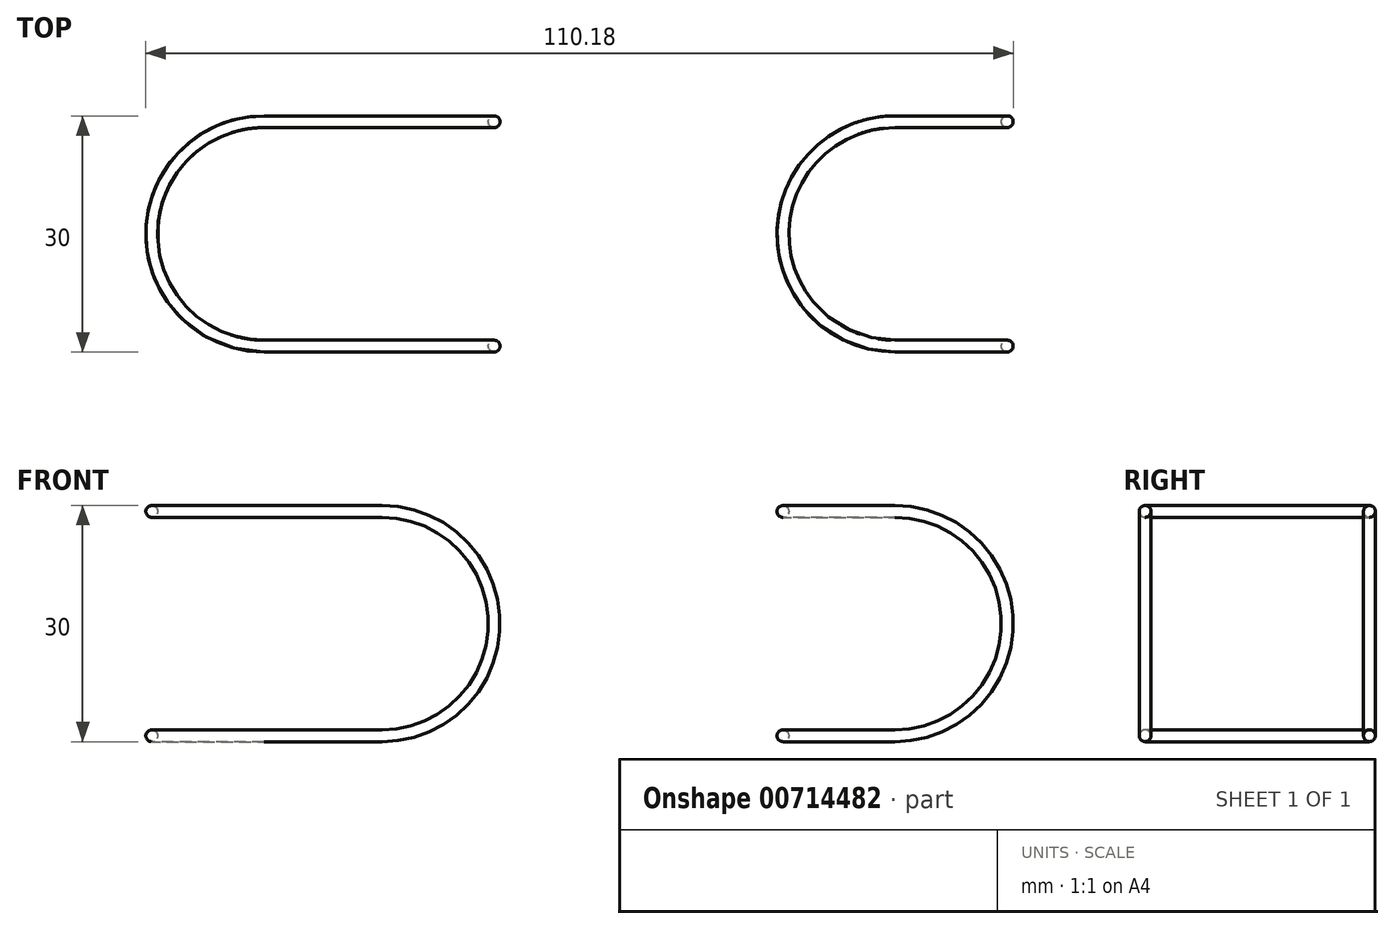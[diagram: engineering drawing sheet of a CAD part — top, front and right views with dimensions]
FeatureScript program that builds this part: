
annotation { "Feature Type Name" : "Feature", "Feature Type Description" : "" }
export const myFeature = defineFeature(function(context is Context, id is Id, definition is map)
    precondition{}
    {
        {
            var Q0;
            Q0=qCreatedBy(makeId("Front.planeOp"),FACE);
            var sketch = newSketch(context, id + "F0", { "sketchPlane" : qUnion([Q0])});
            skArc(sketch, "E0", {"start": v(0, -15) * mm, "mid": v(15, 0) * mm, "end": v(0, 15) * mm});
            skLineSegment(sketch, "E1", {"start": v(0, 15) * mm, "end": v(-30, 15) * mm});
            skLineSegment(sketch, "E2", {"start": v(0, -15) * mm, "end": v(-30, -15) * mm});
            skLineSegment(sketch, "E3", {"start": v(-30, -15) * mm, "end": v(-30, 15) * mm});
            skSolve(sketch);
        }
        {
            var Q0;
            Q0 = qSketchRegion(id + "F0", true);
            extrude(context, id + "F1", {"entities" : qUnion([Q0]), "endBound" : BoundingType.SYMMETRIC, "depth" : 30 * mm, "offsetDistance" : 25 * mm});
        }
        {
            var Q0;
            Q0=makeQuery(id+"F1.opExtrude","CAP_EDGE",EDGE,{"disambiguationData":[OSD([sQuery(id+"F0.wireOp",EDGE,"E3")])],"isStart":false});
            var Q1;
            Q1=makeQuery(id+"F1.opExtrude","CAP_EDGE",EDGE,{"disambiguationData":[OSD([sQuery(id+"F0.wireOp",EDGE,"E3")])],"isStart":true});
            fillet(context, id + "F2", {"entities" : qUnion([Q0, Q1]), "radius" : 15 * mm, "tangentPropagation" : true, "allowEdgeOverflow" : false});
        }
        {
            var Q0;
            Q0=makeQuery(id+"F1.opExtrude","SWEPT_FACE",FACE,{"disambiguationData":[OSD([sQuery(id+"F0.wireOp",EDGE,"E0")])]});
            var Q1;
            Q1=makeQuery(id+"F1.opExtrude","SWEPT_FACE",FACE,{"disambiguationData":[OSD([sQuery(id+"F0.wireOp",EDGE,"E2")])]});
            var Q2;
            Q2=makeQuery(id+"F1.opExtrude","SWEPT_FACE",FACE,{"disambiguationData":[OSD([sQuery(id+"F0.wireOp",EDGE,"E1")])]});
            shell(context, id + "F3", {"entities" : qUnion([Q0, Q1, Q2]), "thickness" : 1.5 * mm});
        }
        {
            var Q0;
            Q0=qCreatedBy(makeId("Front.planeOp"),FACE);
            var sketch = newSketch(context, id + "F4", { "sketchPlane" : qUnion([Q0])});
            skArc(sketch, "E4.0", {"start": v(0, -15) * mm, "mid": v(15, 0) * mm, "end": v(0, 15) * mm, "construction": true});
            skLineSegment(sketch, "E4.1", {"start": v(0, -15) * mm, "end": v(-15, -15) * mm, "construction": true});
            skLineSegment(sketch, "E4.2", {"start": v(0, 15) * mm, "end": v(-15, 15) * mm, "construction": true});
            skLineSegment(sketch, "E4.3", {"start": v(-15, 15) * mm, "end": v(-30, 15) * mm, "construction": true});
            skLineSegment(sketch, "E4.4", {"start": v(-15, -15) * mm, "end": v(-30, -15) * mm, "construction": true});
            skLineSegment(sketch, "E5.0", {"start": v(-15, 13.5) * mm, "end": v(-30, 13.5) * mm});
            skLineSegment(sketch, "E5.1", {"start": v(-15, -13.5) * mm, "end": v(-30, -13.5) * mm});
            skLineSegment(sketch, "E5.2", {"start": v(0, -13.5) * mm, "end": v(-15, -13.5) * mm});
            skArc(sketch, "E5.3", {"start": v(0, -13.5) * mm, "mid": v(13.5, 0) * mm, "end": v(0, 13.5) * mm});
            skLineSegment(sketch, "E5.4", {"start": v(0, 13.5) * mm, "end": v(-15, 13.5) * mm});
            skLineSegment(sketch, "E6", {"start": v(-30, -13.5) * mm, "end": v(-30, 13.5) * mm});
            skSolve(sketch);
        }
        {
            var Q0;
            Q0=makeQuery(id+"F4.imprint","IMPRINT",FACE,{"disambiguationData":[TD([[makeQuery(id+"F4.imprint","IMPRINT",EDGE,{"derivedFrom":sQuery(id+"F4.wireOp",EDGE,"E5.0")}),1.0]])]});
            extrude(context, id + "F5", {"entities" : qUnion([Q0]), "operationType" : NewBodyOperationType.REMOVE, "endBound" : BoundingType.SYMMETRIC, "depth" : 35 * mm, "offsetDistance" : 25 * mm});
        }
        {
            var Q0;
            Q0=makeQuery(id+"F1.opExtrude","CAP_EDGE",EDGE,{"disambiguationData":[OSD([sQuery(id+"F0.wireOp",EDGE,"E1")])],"isStart":true});
            var Q1;
            Q1=makeQuery(id+"F5.boolean.opBoolean","INTERSECT",EDGE,{"derivedFrom":[makeQuery(id+"F1.opExtrude","CAP_FACE",FACE,{"disambiguationData":[OSD([sQuery(id+"F0.wireOp",EDGE,"E0"),sQuery(id+"F0.wireOp",EDGE,"E1"),sQuery(id+"F0.wireOp",EDGE,"E2"),sQuery(id+"F0.wireOp",EDGE,"E3")])],"isStart":true}),makeQuery(id+"F5.opExtrude","SWEPT_FACE",FACE,{"disambiguationData":[OSD([sQuery(id+"F4.wireOp",EDGE,"E5.0"),sQuery(id+"F4.wireOp",EDGE,"E5.4")])]})]});
            var Q2;
            {var subQ0=sQuery(id+"F0.wireOp",EDGE,"E2");Q2=makeQuery(id+"F3.opShell","OFFSET_EDGE",EDGE,{"disambiguationData":[OSD([subQ0]),TDD([makeQuery(id+"F1.opExtrude","CAP_EDGE",EDGE,{"disambiguationData":[OSD([subQ0])],"isStart":false})])]});}
            var Q3;
            {var subQ0=sQuery(id+"F0.wireOp",EDGE,"E3");var subQ1=sQuery(id+"F0.wireOp",EDGE,"E2");var subQ2=sQuery(id+"F0.wireOp",EDGE,"E1");var subQ3=sQuery(id+"F0.wireOp",EDGE,"E0");Q3=makeQuery(id+"F5.boolean.opBoolean","INTERSECT",EDGE,{"derivedFrom":[makeQuery(id+"F3.opShell","OFFSET_FACE",FACE,{"disambiguationData":[OSD([subQ3,subQ2,subQ1,subQ0]),TDD([makeQuery(id+"F1.opExtrude","CAP_FACE",FACE,{"disambiguationData":[OSD([subQ3,subQ2,subQ1,subQ0])],"isStart":false})])]}),makeQuery(id+"F5.opExtrude","SWEPT_FACE",FACE,{"disambiguationData":[OSD([sQuery(id+"F4.wireOp",EDGE,"E5.0"),sQuery(id+"F4.wireOp",EDGE,"E5.4")])]})]});}
            fillet(context, id + "F6", {"entities" : qUnion([Q0, Q1, Q2, Q3]), "radius" : .75 * mm, "tangentPropagation" : true, "allowEdgeOverflow" : false});
        }
        {
            var Q0;
            Q0=qCreatedBy(makeId("Front.planeOp"),FACE);
            var sketch = newSketch(context, id + "F7", { "sketchPlane" : qUnion([Q0])});
            skArc(sketch, "E7", {"start": v(65.18, -15) * mm, "mid": v(80.18, 0) * mm, "end": v(65.18, 15) * mm});
            skLineSegment(sketch, "E8", {"start": v(65.18, 15) * mm, "end": v(50.18, 15) * mm});
            skLineSegment(sketch, "E9", {"start": v(50.18, -15) * mm, "end": v(65.18, -15) * mm});
            skLineSegment(sketch, "E10", {"start": v(50.18, 15) * mm, "end": v(50.18, -15) * mm});
            skSolve(sketch);
        }
        {
            var Q0;
            Q0=makeQuery(id+"F7.imprint","IMPRINT",FACE,{"disambiguationData":[TD([[makeQuery(id+"F7.imprint","IMPRINT",EDGE,{"derivedFrom":sQuery(id+"F7.wireOp",EDGE,"E7")}),1.0]])]});
            extrude(context, id + "F8", {"entities" : qUnion([Q0]), "endBound" : BoundingType.SYMMETRIC, "depth" : 30 * mm, "offsetDistance" : 25 * mm});
        }
        {
            var Q0;
            Q0=makeQuery(id+"F8.opExtrude","CAP_EDGE",EDGE,{"disambiguationData":[OSD([sQuery(id+"F7.wireOp",EDGE,"E10")])],"isStart":true});
            var Q1;
            Q1=makeQuery(id+"F8.opExtrude","CAP_EDGE",EDGE,{"disambiguationData":[OSD([sQuery(id+"F7.wireOp",EDGE,"E10")])],"isStart":false});
            fillet(context, id + "F9", {"entities" : qUnion([Q0, Q1]), "radius" : 15 * mm, "tangentPropagation" : true, "allowEdgeOverflow" : false});
        }
        {
            var Q0;
            Q0=makeQuery(id+"F8.opExtrude","CAP_FACE",FACE,{"disambiguationData":[OSD([sQuery(id+"F7.wireOp",EDGE,"E7"),sQuery(id+"F7.wireOp",EDGE,"E8"),sQuery(id+"F7.wireOp",EDGE,"E9"),sQuery(id+"F7.wireOp",EDGE,"E10")])],"isStart":true});
            var Q1;
            Q1=makeQuery(id+"F9.opFillet","BLEND_FACE",FACE,{"disambiguationData":[OSD([sQuery(id+"F7.wireOp",EDGE,"E10")])]});
            var Q2;
            Q2=makeQuery(id+"F8.opExtrude","CAP_FACE",FACE,{"disambiguationData":[OSD([sQuery(id+"F7.wireOp",EDGE,"E7"),sQuery(id+"F7.wireOp",EDGE,"E8"),sQuery(id+"F7.wireOp",EDGE,"E9"),sQuery(id+"F7.wireOp",EDGE,"E10")])],"isStart":false});
            shell(context, id + "F10", {"entities" : qUnion([Q0, Q1, Q2]), "thickness" : 1.5 * mm});
        }
        {
            var Q0;
            Q0=makeQuery(id+"F8.opExtrude","SWEPT_FACE",FACE,{"disambiguationData":[OSD([sQuery(id+"F7.wireOp",EDGE,"E7")])]});
            var Q1;
            Q1=makeQuery(id+"F8.opExtrude","SWEPT_FACE",FACE,{"disambiguationData":[OSD([sQuery(id+"F7.wireOp",EDGE,"E9")])]});
            var Q2;
            Q2=makeQuery(id+"F8.opExtrude","SWEPT_FACE",FACE,{"disambiguationData":[OSD([sQuery(id+"F7.wireOp",EDGE,"E8")])]});
            shell(context, id + "F11", {"entities" : qUnion([Q0, Q1, Q2]), "thickness" : 1.5 * mm});
        }
        {
            var Q0;
            Q0=qCreatedBy(makeId("Top.planeOp"),FACE);
            var sketch = newSketch(context, id + "F12", { "sketchPlane" : qUnion([Q0])});
            skLineSegment(sketch, "E11.0", {"start": v(65.18, 15) * mm, "end": v(80.18, 15) * mm, "construction": true});
            skArc(sketch, "E12.0", {"start": v(65.18, 15) * mm, "mid": v(50.18, 0) * mm, "end": v(65.18, -15) * mm, "construction": true});
            skLineSegment(sketch, "E13.0", {"start": v(65.18, -15) * mm, "end": v(80.18, -15) * mm, "construction": true});
            skLineSegment(sketch, "E14.0", {"start": v(65.18, 13.5) * mm, "end": v(80.18, 13.5) * mm});
            skArc(sketch, "E14.1", {"start": v(65.18, 13.5) * mm, "mid": v(51.68, 0) * mm, "end": v(65.18, -13.5) * mm});
            skLineSegment(sketch, "E14.2", {"start": v(65.18, -13.5) * mm, "end": v(80.18, -13.5) * mm});
            skLineSegment(sketch, "E15", {"start": v(80.18, 13.5) * mm, "end": v(80.18, -13.5) * mm});
            skSolve(sketch);
        }
        {
            var Q0;
            Q0 = qSketchRegion(id + "F12", true);
            extrude(context, id + "F13", {"entities" : qUnion([Q0]), "operationType" : NewBodyOperationType.REMOVE, "endBound" : BoundingType.SYMMETRIC, "oppositeDirection" : true, "depth" : 30 * mm, "offsetDistance" : 25 * mm});
        }
        {
            var Q0;
            Q0=makeQuery(id+"F13.boolean.opBoolean","INTERSECT",EDGE,{"derivedFrom":[makeQuery(id+"F8.opExtrude","SWEPT_FACE",FACE,{"disambiguationData":[OSD([sQuery(id+"F7.wireOp",EDGE,"E7")])]}),makeQuery(id+"F13.opExtrude","SWEPT_FACE",FACE,{"disambiguationData":[OSD([sQuery(id+"F12.wireOp",EDGE,"E14.2")])]})]});
            var Q1;
            Q1=makeQuery(id+"F8.opExtrude","CAP_EDGE",EDGE,{"disambiguationData":[OSD([sQuery(id+"F7.wireOp",EDGE,"E7")])],"isStart":false});
            var Q2;
            {var subQ0=sQuery(id+"F7.wireOp",EDGE,"E7");Q2=makeQuery(id+"F10.opShell","OFFSET_EDGE",EDGE,{"disambiguationData":[OSD([subQ0]),TDD([makeQuery(id+"F8.opExtrude","CAP_EDGE",EDGE,{"disambiguationData":[OSD([subQ0])],"isStart":true})])]});}
            var Q3;
            Q3=makeQuery(id+"F13.boolean.opBoolean","INTERSECT",EDGE,{"derivedFrom":[makeQuery(id+"F10.opShell","OFFSET_FACE",FACE,{"disambiguationData":[OSD([sQuery(id+"F7.wireOp",EDGE,"E7")])]}),makeQuery(id+"F13.opExtrude","SWEPT_FACE",FACE,{"disambiguationData":[OSD([sQuery(id+"F12.wireOp",EDGE,"E14.2")])]})]});
            fillet(context, id + "F14", {"entities" : qUnion([Q0, Q1, Q2, Q3]), "radius" : .75 * mm, "tangentPropagation" : true, "allowEdgeOverflow" : false});
        }
    });
